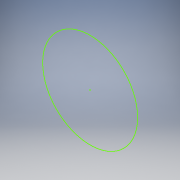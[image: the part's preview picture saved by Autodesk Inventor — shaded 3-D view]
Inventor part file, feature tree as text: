
AUTODESK INVENTOR PART (.ipt)
format: ipt  version: 2017 (Build 210142000, 142)  size: 80,896 bytes
history: native  units: in
note: dims shown in document units (in); Inventor stores cm internally (conversion verified against a paired STEP export)
features: sketch x1
ambient origin geometry x8: Origin, YZ Plane, XZ Plane, XY Plane, X Axis, Y Axis, Z Axis, Center Point
feature tree (1):
  sketch  "Sketch1"
